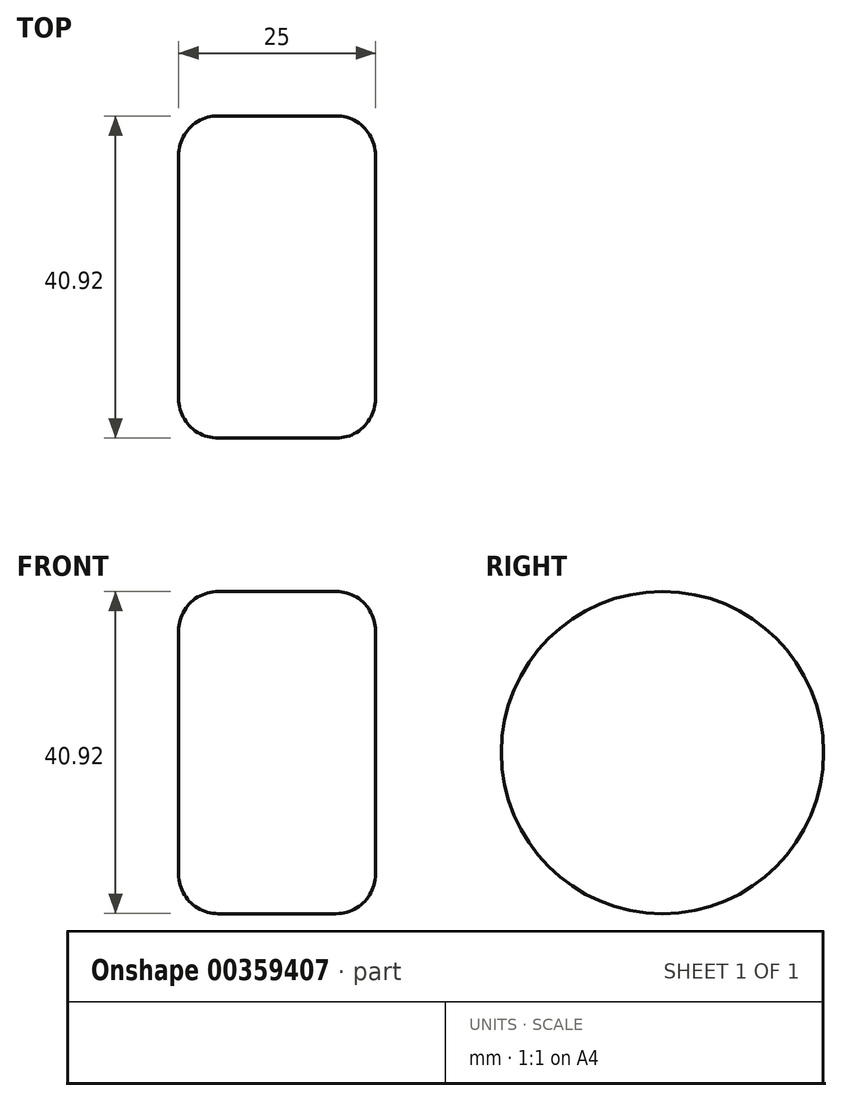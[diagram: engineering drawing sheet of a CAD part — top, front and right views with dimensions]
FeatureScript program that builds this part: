
annotation { "Feature Type Name" : "Feature", "Feature Type Description" : "" }
export const myFeature = defineFeature(function(context is Context, id is Id, definition is map)
    precondition{}
    {
        {
            var Q0;
            Q0=qCreatedBy(makeId("Right.planeOp"),FACE);
            var sketch = newSketch(context, id + "F0", { "sketchPlane" : qUnion([Q0])});
            skCircle(sketch, "E0", {"center": v(0, 0) * mm, "radius": 20.46 * mm});
            skSolve(sketch);
        }
        {
            var Q0;
            Q0=makeQuery(id+"F0.imprint","IMPRINT",FACE,{"disambiguationData":[TD([[makeQuery(id+"F0.imprint","IMPRINT",EDGE,{"derivedFrom":sQuery(id+"F0.wireOp",EDGE,"E0")}),1.0]])]});
            extrude(context, id + "F1", {"entities" : qUnion([Q0]), "depth" : 25 * mm});
        }
        {
            var Q0;
            Q0=makeQuery(id+"F1.opExtrude","CAP_EDGE",EDGE,{"disambiguationData":[OSD([sQuery(id+"F0.wireOp",EDGE,"E0")])],"isStart":false});
            var Q1;
            Q1=makeQuery(id+"F1.opExtrude","CAP_EDGE",EDGE,{"disambiguationData":[OSD([sQuery(id+"F0.wireOp",EDGE,"E0")])],"isStart":true});
            fillet(context, id + "F2", {"entities" : qUnion([Q0, Q1]), "radius" : 5 * mm, "tangentPropagation" : true, "allowEdgeOverflow" : false});
        }
        {
            var Q0;
            Q0=qCreatedBy(makeId("Right.planeOp"),FACE);
            cPlane(context, id + "F3", {"entities" : qUnion([Q0]), "cplaneType" : CPlaneType.OFFSET, "offset" : 200 * mm, "width" : 150 * mm, "height" : 150 * mm});
        }
    });
